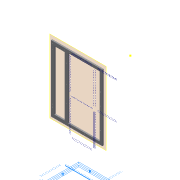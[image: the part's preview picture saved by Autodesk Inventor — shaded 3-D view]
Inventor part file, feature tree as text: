
AUTODESK INVENTOR PART (.ipt)
format: ipt  version: 2019.4 (Build 234330000, 330)  size: 311,808 bytes
history: native  units: mm
features: projected_geometry x4, sketch x3, other x3, extrude x2, hole x2, plane x1
ambient origin geometry x8: Origin, YZ Plane, XZ Plane, XY Plane, X Axis, Y Axis, Z Axis, Center Point
bodies: Body1 (feature_tree)
feature tree (15):
  plane  "Work Plane3"
  extrude  "Extrusion3"  Depth=2.0mm
  hole  "Hole2"  [1 undecoded]
  extrude  "Extrusion4"  Depth=5.0mm
  hole  "Hole3"  [1 undecoded]
  sketch  "Sketch6"  dims[d11=5.0mm d12=0.0mm]
  sketch  "Sketch8"  dims[d13=2.8mm d14=6.0mm d15=4.0mm d16=2.0mm d17=90.0deg d18=8.0mm d19=20.594885mm d20=1.0mm]
  projected_geometry  "Projected Loop3"
  sketch  "Sketch10"  dims[d21=1.0mm d22=1.0mm d23=1.0mm d24=1.0mm d25=10.0mm d26=0.0mm d27=2.8mm d28=6.0mm d29=6.0mm d30=5.0mm d31=90.0deg d32=8.0mm d33=20.594885mm]
  projected_geometry  "Projected Loop4"
  projected_geometry  "Projected Loop5"
  projected_geometry  "Projected Loop6"
  other  "Assembly_Opentrons_Imagingunit_v3.iam"
  other  "Assembly_opentrons_microscope_slide_y_base:1"
  other  "02_Opentrons_Microscope_Base_v0:1"
note: 2 required parameter values undecoded (feature->parameter linkage not recoverable at this tier; creation-order binding heuristic only, values carry confidence <= 0.55)
